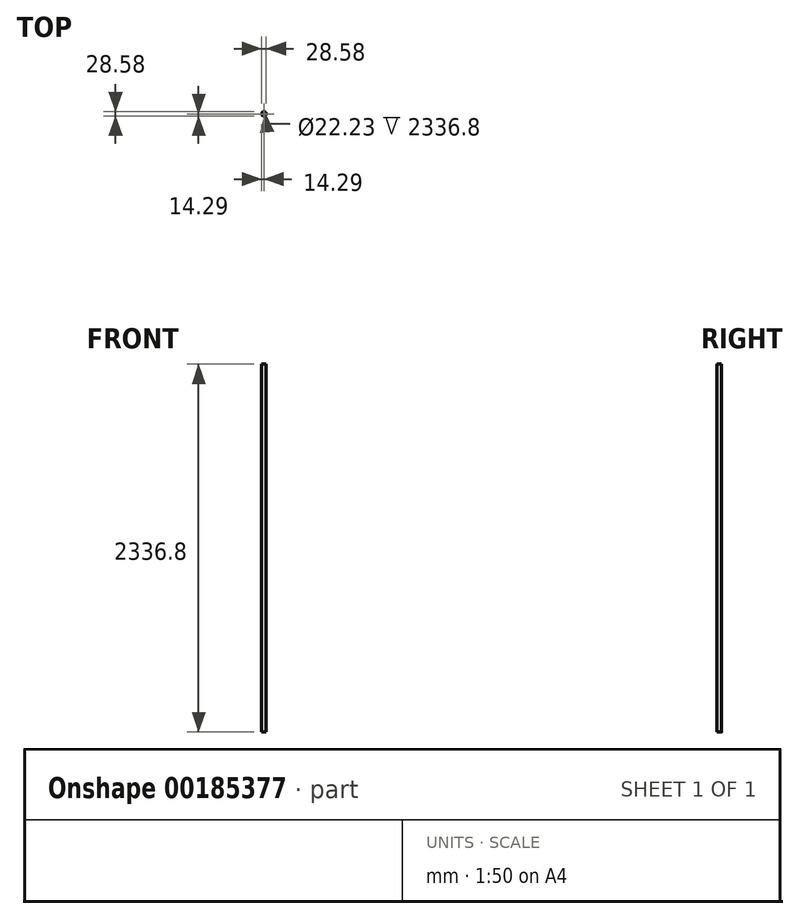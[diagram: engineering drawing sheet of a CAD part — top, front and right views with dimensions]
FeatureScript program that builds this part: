
annotation { "Feature Type Name" : "Feature", "Feature Type Description" : "" }
export const myFeature = defineFeature(function(context is Context, id is Id, definition is map)
    precondition{}
    {
        {
            var Q0;
            Q0=qCreatedBy(makeId("Top.planeOp"),FACE);
            var sketch = newSketch(context, id + "F0", { "sketchPlane" : qUnion([Q0])});
            skCircle(sketch, "E0", {"center": v(0, 0) * mm, "radius": 14.29 * mm});
            skCircle(sketch, "E1", {"center": v(0, 0) * mm, "radius": 11.11 * mm});
            skSolve(sketch);
        }
        {
            var Q0;
            Q0=makeQuery(id+"F0.imprint","IMPRINT",FACE,{"disambiguationData":[TD([[makeQuery(id+"F0.imprint","IMPRINT",EDGE,{"derivedFrom":sQuery(id+"F0.wireOp",EDGE,"E0")}),1.0]])]});
            extrude(context, id + "F1", {"entities" : qUnion([Q0]), "depth" : 2336.8 * mm});
        }
    });
